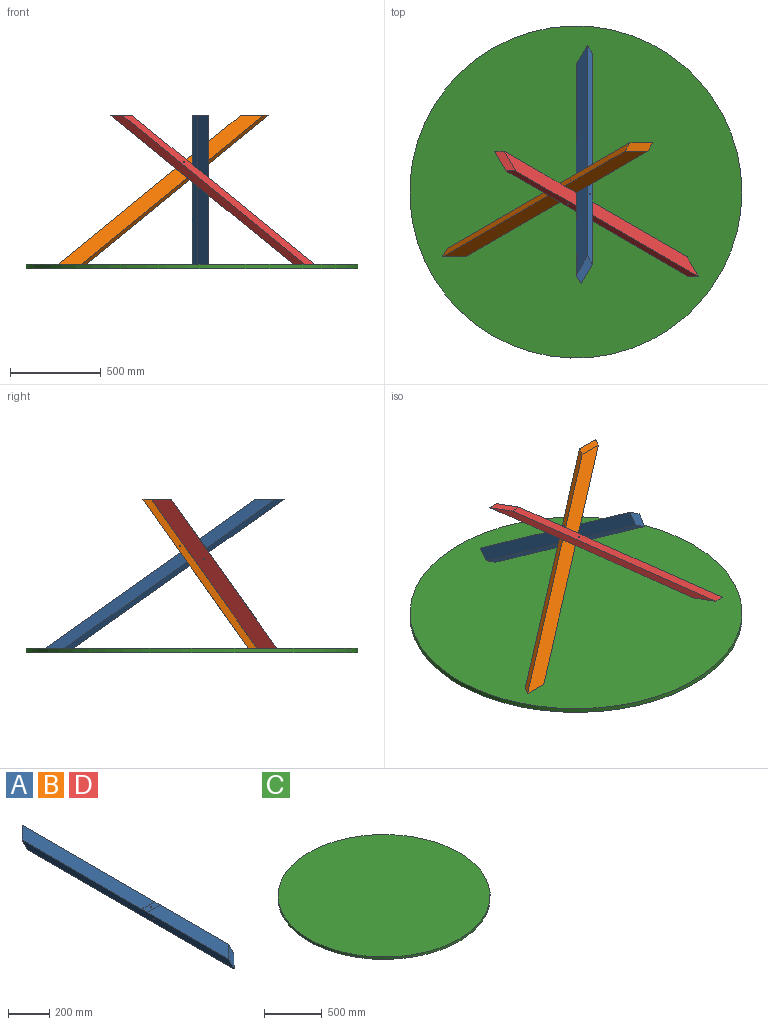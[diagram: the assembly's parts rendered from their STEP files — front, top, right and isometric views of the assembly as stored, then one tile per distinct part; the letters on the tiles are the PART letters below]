
ASSEMBLY  parts=4 mates=5
PART A: 12 faces, bbox 88.9x1549.4x38.1 mm
  f0: plane 914.4x88.9mm, normal (0,0,1), area 77338.6mm2, adj f1,f4,f6,f10
  f1: plane 1460.5x38.1mm, normal (-1,0,0), area 54160.8mm2, adj f0,f3,f5,f6,f7,f8,f9,f10
  f2: cylinder r=3.17mm len=38.07mm, axis (0,0,1), area 759.6mm2, adj f3,f9
  f3: plane 1511.3x88.9mm, normal (0,0,-1), area 126419.7mm2, adj f1,f2,f4,f6,f7
  f4: plane 1460.5x38.1mm, normal (1,0,0), area 54160.8mm2, adj f0,f3,f5,f6,f7,f8,f9,f10
  f5: plane 558.8x88.9mm, normal (0,0,1), area 45725.7mm2, adj f1,f4,f7,f11
  f6: plane 127x88.9mm, normal (-0.58,0.58,-0.58), area 5866.6mm2, adj f0,f1,f3,f4
  f7: plane 127x88.9mm, normal (0.58,-0.58,0.58), area 5866.6mm2, adj f1,f3,f4,f5
  f8: cylinder r=3.17mm len=88.9mm, axis (-1,0,0), area 1773.5mm2, adj f1,f4
  f9: plane 88.9x38.1mm, normal (0,0,1), area 3355.4mm2, adj f1,f2,f4,f10,f11
  f10: plane 88.9x0.03mm, normal (0,-1,0), area 2.3mm2, adj f0,f1,f4,f9
  f11: plane 88.9x0.03mm, normal (0,1,0), area 2.3mm2, adj f1,f4,f5,f9
PART B: same geometry as A
PART C: 3 faces, bbox 1828.8x1828.8x25.4 mm
  f0: cylinder r=914.4mm len=1828.8mm, axis (0,0,1), area 145931.8mm2, adj f1,f2
  f1: plane 1828.8x1828.8mm, normal (0,0,-1), area 2626771.6mm2, adj f0
  f2: plane 1828.8x1828.8mm, normal (0,0,1), area 2626771.6mm2, adj f0
PART D: same geometry as A
PLACE A rot(axis=(-0.59,-0.77,0.24),56.6deg) t=(-199.89,235.53,461.61)mm
PLACE B rot(axis=(0.19,-0.45,0.87),140.3deg) t=(-253.77,235.53,461.61)mm
PLACE C t=(381.25,-384.65,7)mm fixed
PLACE D rot(axis=(-0.54,0.07,-0.84),114.5deg) t=(-226.83,188.87,461.61)mm
MATE parallel B.f6 <-> C.f0  axis (0,0,-1) through (-886.88,-109.25,7)mm
MATE cylindrical A.f8 <-> D.f2  axis (-0.71,-0.41,-0.58) through (-213.36,175.91,520.27)mm
MATE cylindrical A.f2 <-> B.f8  axis (-0.71,0.41,0.58) through (-195.4,253.68,520.27)mm
MATE planar D.f6 <-> C.f0  axis (0,0,-1) through (388.32,-187.02,7)mm
MATE cylindrical D.f8 <-> B.f2  axis (0,0.82,-0.58) through (-271.73,230.35,520.27)mm
